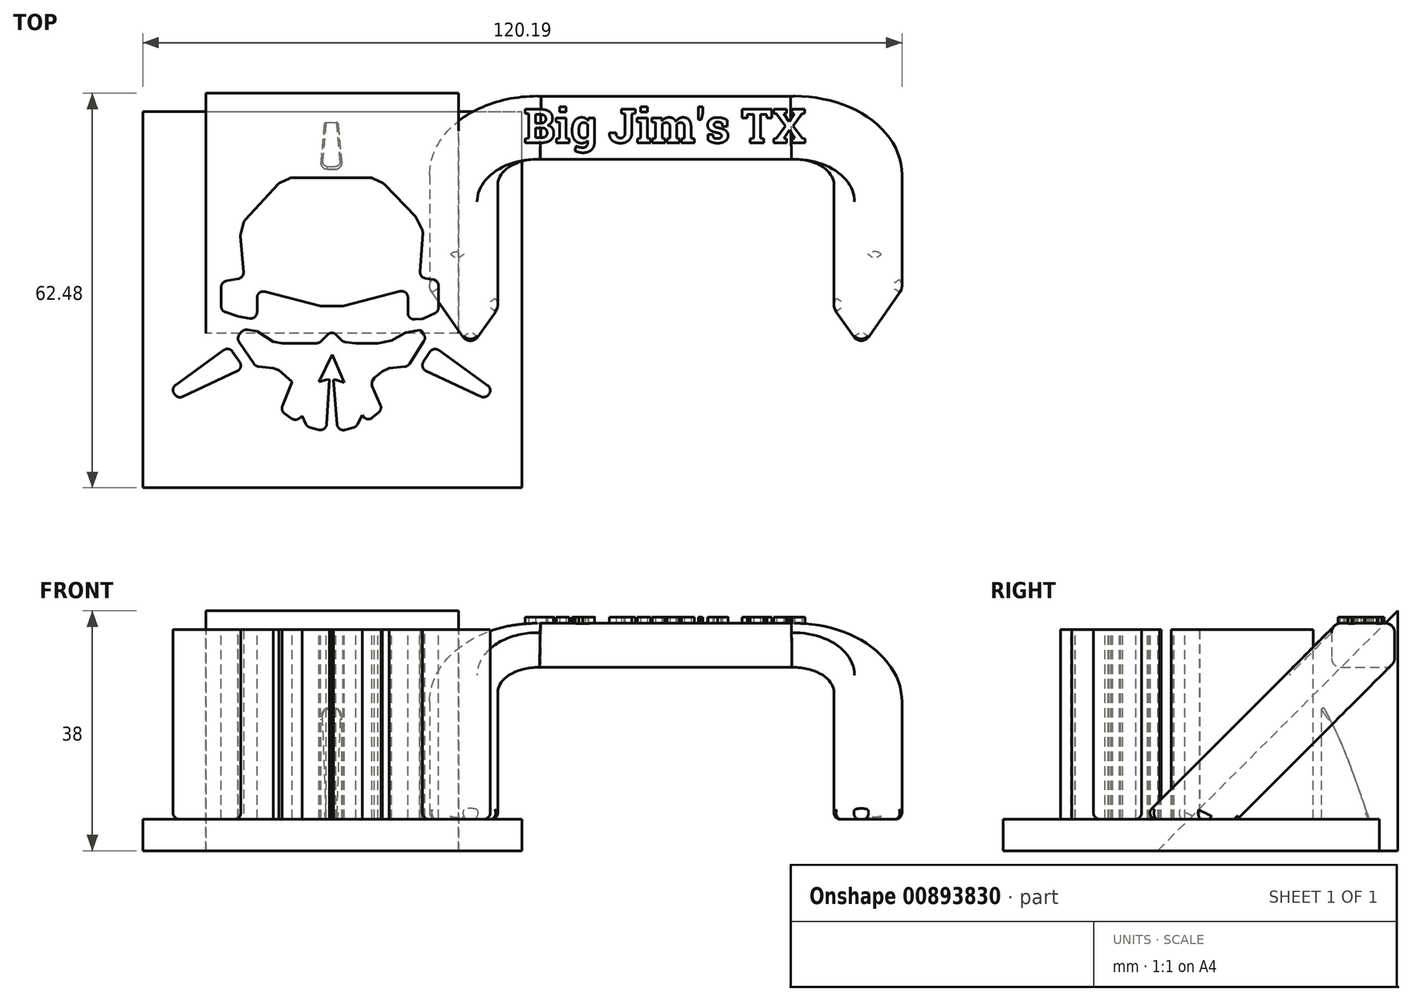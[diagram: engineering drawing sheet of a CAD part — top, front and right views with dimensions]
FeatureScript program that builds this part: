
annotation { "Feature Type Name" : "Feature", "Feature Type Description" : "" }
export const myFeature = defineFeature(function(context is Context, id is Id, definition is map)
    precondition{}
    {
        {
            var Q0;
            Q0=qCreatedBy(makeId("Front.planeOp"),FACE);
            var sketch = newSketch(context, id + "F0", { "sketchPlane" : qUnion([Q0])});
            skLineSegment(sketch, "E0", {"start": v(0, 0) * mm, "end": v(24, 0) * mm});
            skLineSegment(sketch, "E1", {"start": v(27, 5) * mm, "end": v(24, 0) * mm});
            skLineSegment(sketch, "E2", {"start": v(27, 5) * mm, "end": v(28.5, 5) * mm});
            skLineSegment(sketch, "E3", {"start": v(0, 35) * mm, "end": v(0, 0) * mm});
            skFitSpline(sketch, "E4", {"points": [v(0, 35) * mm, v(9.06, 34) * mm, v(13.03, 32.01) * mm, v(20.35, 24.23) * mm, v(28.5, 5) * mm], "startDerivative": vector(43.74, -2.76) * mm, "endDerivative": vector(20.52, -60.26) * mm});
            skSolve(sketch);
        }
        {
            var Q0;
            Q0=qSketchRegion(id+"F0",true);
            var Q1;
            Q1=sQuery(id+"F0.wireOp",EDGE,"E3");
            revolve(context, id + "F1", {"entities" : qUnion([Q0]), "axis" : qUnion([Q1]), "revolveType" : RevolveType.FULL});
        }
        {
            var Q0;
            Q0=qCreatedBy(makeId("Top.planeOp"),FACE);
            var sketch = newSketch(context, id + "F2", { "sketchPlane" : qUnion([Q0])});
            skCircle(sketch, "E5", {"center": v(0, 0) * mm, "radius": 5 * mm});
            skSolve(sketch);
        }
        {
            var Q0;
            Q0=qSketchRegion(id+"F2",true);
            extrude(context, id + "F3", {"entities" : qUnion([Q0]), "depth" : 32 * mm});
        }
        {
            var Q0;
            Q0=makeQuery(id+"F3.opExtrude","SWEPT_BODY",BODY,{"disambiguationData":[OSD([sQuery(id+"F2.wireOp",EDGE,"E5")])]});
            var Q1;
            Q1=makeQuery(id+"F1.opRevolve","SWEPT_BODY",BODY,{"disambiguationData":[OSD([sQuery(id+"F0.wireOp",EDGE,"E0"),sQuery(id+"F0.wireOp",EDGE,"E1"),sQuery(id+"F0.wireOp",EDGE,"E2"),sQuery(id+"F0.wireOp",EDGE,"3aklZLSy-hCqH-fZIi-s1VG-uW10MH76g0WD"),sQuery(id+"F0.wireOp",EDGE,"wuCtKPpf-We7b-kOsq-7vQO-teLjAkYNJH5X"),sQuery(id+"F0.wireOp",EDGE,"E3")])]});
            booleanBodies(context, id + "F4", {"operationType" : BooleanOperationType.SUBTRACTION, "tools" : qUnion([Q0]), "targets" : qUnion([Q1])});
        }
        {
            var Q0;
            Q0=qCreatedBy(makeId("Top.planeOp"),FACE);
            cPlane(context, id + "F5", {"entities" : qUnion([Q0]), "cplaneType" : CPlaneType.OFFSET, "offset" : 35 * mm, "width" : 150 * mm, "height" : 150 * mm});
        }
        {
            var Q0;
            Q0=qCreatedBy(id+"F5.planeOp",FACE);
            var sketch = newSketch(context, id + "F6", { "sketchPlane" : qUnion([Q0])});
            skLineSegment(sketch, "E6", {"start": v(-1.9, 20.95) * mm, "end": v(1.57, 20.95) * mm});
            skLineSegment(sketch, "E7", {"start": v(1.57, 20.95) * mm, "end": v(0.85, 28.83) * mm});
            skLineSegment(sketch, "E8", {"start": v(0.85, 28.83) * mm, "end": v(-1.17, 28.83) * mm});
            skLineSegment(sketch, "E9", {"start": v(-1.17, 28.83) * mm, "end": v(-1.9, 20.95) * mm});
            skLineSegment(sketch, "E10", {"start": v(-16.39, -7.1) * mm, "end": v(-14, -10.52) * mm});
            skLineSegment(sketch, "E11", {"start": v(-14, -10.52) * mm, "end": v(-24.43, -15.42) * mm});
            skLineSegment(sketch, "E12", {"start": v(-24.43, -15.42) * mm, "end": v(-25.63, -13.79) * mm});
            skLineSegment(sketch, "E13", {"start": v(-25.63, -13.79) * mm, "end": v(-16.39, -7.1) * mm});
            skLineSegment(sketch, "E14", {"start": v(16, -7.1) * mm, "end": v(13.8, -10.52) * mm});
            skLineSegment(sketch, "E15", {"start": v(13.8, -10.52) * mm, "end": v(24.28, -15.42) * mm});
            skLineSegment(sketch, "E16", {"start": v(24.28, -15.42) * mm, "end": v(25.36, -13.83) * mm});
            skLineSegment(sketch, "E17", {"start": v(25.36, -13.83) * mm, "end": v(16, -7.1) * mm});
            skLineSegment(sketch, "E18", {"start": v(-14, -4.39) * mm, "end": v(-11.93, -4.7) * mm});
            skLineSegment(sketch, "E19", {"start": v(-11.93, -4.7) * mm, "end": v(-9.33, -6.37) * mm});
            skLineSegment(sketch, "E20", {"start": v(-9.33, -6.37) * mm, "end": v(-7.9, -6.6) * mm});
            skLineSegment(sketch, "E21", {"start": v(-7.9, -6.6) * mm, "end": v(-4.54, -6.6) * mm});
            skLineSegment(sketch, "E22", {"start": v(-4.54, -6.6) * mm, "end": v(-2.11, -6.6) * mm});
            skLineSegment(sketch, "E23", {"start": v(-2.11, -6.6) * mm, "end": v(-0.46, -4.94) * mm});
            skLineSegment(sketch, "E24", {"start": v(-0.46, -4.94) * mm, "end": v(0.27, -4.94) * mm});
            skLineSegment(sketch, "E25", {"start": v(0.27, -4.94) * mm, "end": v(1.71, -6.37) * mm});
            skLineSegment(sketch, "E26", {"start": v(1.71, -6.37) * mm, "end": v(3.7, -6.6) * mm});
            skLineSegment(sketch, "E27", {"start": v(3.7, -6.6) * mm, "end": v(7.21, -6.6) * mm});
            skLineSegment(sketch, "E28", {"start": v(7.21, -6.6) * mm, "end": v(9.38, -6.15) * mm});
            skLineSegment(sketch, "E29", {"start": v(9.38, -6.15) * mm, "end": v(11.55, -4.94) * mm});
            skLineSegment(sketch, "E30", {"start": v(11.55, -4.94) * mm, "end": v(13.8, -4.5) * mm});
            skLineSegment(sketch, "E31", {"start": v(13.8, -4.5) * mm, "end": v(14.13, -4.7) * mm});
            skLineSegment(sketch, "E32", {"start": v(14.13, -4.7) * mm, "end": v(14.83, -5.76) * mm});
            skLineSegment(sketch, "E33", {"start": v(14.83, -5.76) * mm, "end": v(11.96, -10.26) * mm});
            skLineSegment(sketch, "E34", {"start": v(11.96, -10.26) * mm, "end": v(8.97, -10.52) * mm});
            skLineSegment(sketch, "E35", {"start": v(8.97, -10.52) * mm, "end": v(7.91, -11.03) * mm});
            skLineSegment(sketch, "E36", {"start": v(7.91, -11.03) * mm, "end": v(6.67, -12.1) * mm});
            skLineSegment(sketch, "E37", {"start": v(6.67, -12.1) * mm, "end": v(6.27, -12.72) * mm});
            skLineSegment(sketch, "E38", {"start": v(6.27, -12.72) * mm, "end": v(6.27, -13.33) * mm});
            skLineSegment(sketch, "E39", {"start": v(6.27, -13.33) * mm, "end": v(7.92, -17.05) * mm});
            skLineSegment(sketch, "E40", {"start": v(7.92, -17.05) * mm, "end": v(5.6, -19.03) * mm});
            skLineSegment(sketch, "E41", {"start": v(5.6, -19.03) * mm, "end": v(4.72, -18) * mm});
            skLineSegment(sketch, "E42", {"start": v(4.72, -18) * mm, "end": v(3.77, -19.83) * mm});
            skLineSegment(sketch, "E43", {"start": v(3.77, -19.83) * mm, "end": v(0.85, -20.66) * mm});
            skLineSegment(sketch, "E44", {"start": v(0.85, -20.66) * mm, "end": v(0.17, -12.4) * mm});
            skLineSegment(sketch, "E45", {"start": v(0.17, -12.4) * mm, "end": v(0.54, -12.37) * mm});
            skLineSegment(sketch, "E46", {"start": v(0.54, -12.37) * mm, "end": v(1.91, -12.83) * mm});
            skLineSegment(sketch, "E47", {"start": v(1.91, -12.83) * mm, "end": v(0, -8.41) * mm});
            skLineSegment(sketch, "E48", {"start": v(0, -8.41) * mm, "end": v(-2.11, -12.7) * mm});
            skLineSegment(sketch, "E49", {"start": v(-2.11, -12.7) * mm, "end": v(-0.97, -12.4) * mm});
            skLineSegment(sketch, "E50", {"start": v(-0.97, -12.4) * mm, "end": v(-0.46, -12.36) * mm});
            skLineSegment(sketch, "E51", {"start": v(-0.46, -12.36) * mm, "end": v(-0.97, -20.6) * mm});
            skLineSegment(sketch, "E52", {"start": v(-0.97, -20.6) * mm, "end": v(-3.99, -19.83) * mm});
            skLineSegment(sketch, "E53", {"start": v(-3.99, -19.83) * mm, "end": v(-4.79, -18.1) * mm});
            skLineSegment(sketch, "E54", {"start": v(-4.79, -18.1) * mm, "end": v(-5.8, -19) * mm});
            skLineSegment(sketch, "E55", {"start": v(-5.8, -19) * mm, "end": v(-8.2, -17.27) * mm});
            skLineSegment(sketch, "E56", {"start": v(-8.2, -17.27) * mm, "end": v(-6.4, -12.7) * mm});
            skLineSegment(sketch, "E57", {"start": v(-6.4, -12.7) * mm, "end": v(-8.47, -10.86) * mm});
            skLineSegment(sketch, "E58", {"start": v(-8.47, -10.86) * mm, "end": v(-9.33, -10.52) * mm});
            skLineSegment(sketch, "E59", {"start": v(-9.33, -10.52) * mm, "end": v(-12.14, -10.26) * mm});
            skLineSegment(sketch, "E60", {"start": v(-12.14, -10.26) * mm, "end": v(-15.2, -5.76) * mm});
            skLineSegment(sketch, "E61", {"start": v(-15.2, -5.76) * mm, "end": v(-14, -4.39) * mm});
            skLineSegment(sketch, "E62", {"start": v(-11.93, -2.85) * mm, "end": v(-14.9, -2.39) * mm});
            skLineSegment(sketch, "E63", {"start": v(-14.9, -2.39) * mm, "end": v(-17.6, -1.45) * mm});
            skLineSegment(sketch, "E64", {"start": v(-17.6, -1.45) * mm, "end": v(-17.6, 3.13) * mm});
            skLineSegment(sketch, "E65", {"start": v(-17.6, 3.13) * mm, "end": v(-14, 3.76) * mm});
            skLineSegment(sketch, "E66", {"start": v(-14, 3.76) * mm, "end": v(-14.56, 10.53) * mm});
            skLineSegment(sketch, "E67", {"start": v(-14.56, 10.53) * mm, "end": v(-14, 12.73) * mm});
            skLineSegment(sketch, "E68", {"start": v(-14, 12.73) * mm, "end": v(-8.4, 18.78) * mm});
            skLineSegment(sketch, "E69", {"start": v(-8.4, 18.78) * mm, "end": v(-6.64, 19.6) * mm});
            skLineSegment(sketch, "E70", {"start": v(-6.64, 19.6) * mm, "end": v(6.27, 19.6) * mm});
            skLineSegment(sketch, "E71", {"start": v(6.27, 19.6) * mm, "end": v(8.13, 18.7) * mm});
            skLineSegment(sketch, "E72", {"start": v(8.13, 18.7) * mm, "end": v(13.27, 13.32) * mm});
            skLineSegment(sketch, "E73", {"start": v(13.27, 13.32) * mm, "end": v(14.35, 11.03) * mm});
            skLineSegment(sketch, "E74", {"start": v(14.35, 11.03) * mm, "end": v(13.8, 3.84) * mm});
            skLineSegment(sketch, "E75", {"start": v(13.8, 3.84) * mm, "end": v(16.8, 3.38) * mm});
            skLineSegment(sketch, "E76", {"start": v(16.8, 3.38) * mm, "end": v(16.8, -1.57) * mm});
            skLineSegment(sketch, "E77", {"start": v(16.8, -1.57) * mm, "end": v(14.4, -2.7) * mm});
            skLineSegment(sketch, "E78", {"start": v(14.4, -2.7) * mm, "end": v(11.96, -2.9) * mm});
            skLineSegment(sketch, "E79", {"start": v(11.96, -2.9) * mm, "end": v(11.96, 1.93) * mm});
            skLineSegment(sketch, "E80", {"start": v(11.96, 1.93) * mm, "end": v(1.71, -0.7) * mm});
            skLineSegment(sketch, "E81", {"start": v(1.71, -0.7) * mm, "end": v(-1.9, -0.7) * mm});
            skLineSegment(sketch, "E82", {"start": v(-1.9, -0.7) * mm, "end": v(-11.93, 1.9) * mm});
            skLineSegment(sketch, "E83", {"start": v(-11.93, 1.9) * mm, "end": v(-11.93, -2.85) * mm});
            skSolve(sketch);
        }
        {
            var Q0;
            Q0=qSketchRegion(id+"F6",true);
            extrude(context, id + "F7", {"entities" : qUnion([Q0]), "oppositeDirection" : true, "depth" : 30 * mm});
        }
        {
            var Q0;
            Q0=qCreatedBy(makeId("Right.planeOp"),FACE);
            var sketch = newSketch(context, id + "F8", { "sketchPlane" : qUnion([Q0])});
            skLineSegment(sketch, "E84.bottom", {"start": v(-29.48, 5) * mm, "end": v(30.12, 5) * mm});
            skLineSegment(sketch, "E84.top", {"start": v(-29.48, 0) * mm, "end": v(30.12, 0) * mm});
            skLineSegment(sketch, "E84.left", {"start": v(-29.48, 5) * mm, "end": v(-29.48, 0) * mm});
            skLineSegment(sketch, "E84.right", {"start": v(30.12, 5) * mm, "end": v(30.12, 0) * mm});
            skSolve(sketch);
        }
        {
            var Q0;
            Q0=makeQuery(id+"F7.opExtrude","SWEPT_EDGE",EDGE,{"disambiguationData":[OSD([sQuery(id+"F6.wireOp",EDGE,"E10"),sQuery(id+"F6.wireOp",EDGE,"E11")])]});
            var Q1;
            Q1=makeQuery(id+"F7.opExtrude","SWEPT_EDGE",EDGE,{"disambiguationData":[OSD([sQuery(id+"F6.wireOp",EDGE,"E59"),sQuery(id+"F6.wireOp",EDGE,"E60")])]});
            var Q2;
            Q2=makeQuery(id+"F7.opExtrude","SWEPT_EDGE",EDGE,{"disambiguationData":[OSD([sQuery(id+"F6.wireOp",EDGE,"E60"),sQuery(id+"F6.wireOp",EDGE,"E61")])]});
            var Q3;
            Q3=makeQuery(id+"F7.opExtrude","SWEPT_EDGE",EDGE,{"disambiguationData":[OSD([sQuery(id+"F6.wireOp",EDGE,"E33"),sQuery(id+"F6.wireOp",EDGE,"E34")])]});
            var Q4;
            Q4=makeQuery(id+"F7.opExtrude","SWEPT_EDGE",EDGE,{"disambiguationData":[OSD([sQuery(id+"F6.wireOp",EDGE,"E14"),sQuery(id+"F6.wireOp",EDGE,"E15")])]});
            var Q5;
            Q5=makeQuery(id+"F7.opExtrude","SWEPT_EDGE",EDGE,{"disambiguationData":[OSD([sQuery(id+"F6.wireOp",EDGE,"E39"),sQuery(id+"F6.wireOp",EDGE,"E40")])]});
            var Q6;
            Q6=makeQuery(id+"F7.opExtrude","SWEPT_EDGE",EDGE,{"disambiguationData":[OSD([sQuery(id+"F6.wireOp",EDGE,"E55"),sQuery(id+"F6.wireOp",EDGE,"E56")])]});
            var Q7;
            Q7=makeQuery(id+"F7.opExtrude","SWEPT_EDGE",EDGE,{"disambiguationData":[OSD([sQuery(id+"F6.wireOp",EDGE,"E51"),sQuery(id+"F6.wireOp",EDGE,"E52")])]});
            var Q8;
            Q8=makeQuery(id+"F7.opExtrude","SWEPT_EDGE",EDGE,{"disambiguationData":[OSD([sQuery(id+"F6.wireOp",EDGE,"E43"),sQuery(id+"F6.wireOp",EDGE,"E44")])]});
            var Q9;
            Q9=makeQuery(id+"F7.opExtrude","SWEPT_EDGE",EDGE,{"disambiguationData":[OSD([sQuery(id+"F6.wireOp",EDGE,"E42"),sQuery(id+"F6.wireOp",EDGE,"E43")])]});
            var Q10;
            Q10=makeQuery(id+"F7.opExtrude","SWEPT_EDGE",EDGE,{"disambiguationData":[OSD([sQuery(id+"F6.wireOp",EDGE,"E52"),sQuery(id+"F6.wireOp",EDGE,"E53")])]});
            var Q11;
            Q11=makeQuery(id+"F7.opExtrude","SWEPT_EDGE",EDGE,{"disambiguationData":[OSD([sQuery(id+"F6.wireOp",EDGE,"E54"),sQuery(id+"F6.wireOp",EDGE,"E55")])]});
            var Q12;
            Q12=makeQuery(id+"F7.opExtrude","SWEPT_EDGE",EDGE,{"disambiguationData":[OSD([sQuery(id+"F6.wireOp",EDGE,"E40"),sQuery(id+"F6.wireOp",EDGE,"E41")])]});
            var Q13;
            Q13=makeQuery(id+"F7.opExtrude","SWEPT_EDGE",EDGE,{"disambiguationData":[OSD([sQuery(id+"F6.wireOp",EDGE,"E32"),sQuery(id+"F6.wireOp",EDGE,"E33")])]});
            var Q14;
            Q14=makeQuery(id+"F7.opExtrude","SWEPT_EDGE",EDGE,{"disambiguationData":[OSD([sQuery(id+"F6.wireOp",EDGE,"E14"),sQuery(id+"F6.wireOp",EDGE,"E17")])]});
            var Q15;
            Q15=makeQuery(id+"F7.opExtrude","SWEPT_EDGE",EDGE,{"disambiguationData":[OSD([sQuery(id+"F6.wireOp",EDGE,"E10"),sQuery(id+"F6.wireOp",EDGE,"E13")])]});
            var Q16;
            Q16=makeQuery(id+"F7.opExtrude","SWEPT_EDGE",EDGE,{"disambiguationData":[OSD([sQuery(id+"F6.wireOp",EDGE,"E18"),sQuery(id+"F6.wireOp",EDGE,"E61")])]});
            var Q17;
            Q17=makeQuery(id+"F7.opExtrude","SWEPT_EDGE",EDGE,{"disambiguationData":[OSD([sQuery(id+"F6.wireOp",EDGE,"E22"),sQuery(id+"F6.wireOp",EDGE,"E23")])]});
            var Q18;
            Q18=makeQuery(id+"F7.opExtrude","SWEPT_EDGE",EDGE,{"disambiguationData":[OSD([sQuery(id+"F6.wireOp",EDGE,"E24"),sQuery(id+"F6.wireOp",EDGE,"E25")])]});
            var Q19;
            Q19=makeQuery(id+"F7.opExtrude","SWEPT_EDGE",EDGE,{"disambiguationData":[OSD([sQuery(id+"F6.wireOp",EDGE,"E25"),sQuery(id+"F6.wireOp",EDGE,"E26")])]});
            var Q20;
            Q20=makeQuery(id+"F7.opExtrude","SWEPT_EDGE",EDGE,{"disambiguationData":[OSD([sQuery(id+"F6.wireOp",EDGE,"E29"),sQuery(id+"F6.wireOp",EDGE,"E30")])]});
            var Q21;
            Q21=makeQuery(id+"F7.opExtrude","SWEPT_EDGE",EDGE,{"disambiguationData":[OSD([sQuery(id+"F6.wireOp",EDGE,"E6"),sQuery(id+"F6.wireOp",EDGE,"E7")])]});
            var Q22;
            Q22=makeQuery(id+"F7.opExtrude","SWEPT_EDGE",EDGE,{"disambiguationData":[OSD([sQuery(id+"F6.wireOp",EDGE,"E6"),sQuery(id+"F6.wireOp",EDGE,"E9")])]});
            var Q23;
            Q23=makeQuery(id+"F7.opExtrude","SWEPT_EDGE",EDGE,{"disambiguationData":[OSD([sQuery(id+"F6.wireOp",EDGE,"E69"),sQuery(id+"F6.wireOp",EDGE,"E70")])]});
            var Q24;
            Q24=makeQuery(id+"F7.opExtrude","SWEPT_EDGE",EDGE,{"disambiguationData":[OSD([sQuery(id+"F6.wireOp",EDGE,"E68"),sQuery(id+"F6.wireOp",EDGE,"E69")])]});
            var Q25;
            Q25=makeQuery(id+"F7.opExtrude","SWEPT_EDGE",EDGE,{"disambiguationData":[OSD([sQuery(id+"F6.wireOp",EDGE,"E70"),sQuery(id+"F6.wireOp",EDGE,"E71")])]});
            var Q26;
            Q26=makeQuery(id+"F7.opExtrude","SWEPT_EDGE",EDGE,{"disambiguationData":[OSD([sQuery(id+"F6.wireOp",EDGE,"E71"),sQuery(id+"F6.wireOp",EDGE,"E72")])]});
            var Q27;
            Q27=makeQuery(id+"F7.opExtrude","SWEPT_EDGE",EDGE,{"disambiguationData":[OSD([sQuery(id+"F6.wireOp",EDGE,"E67"),sQuery(id+"F6.wireOp",EDGE,"E68")])]});
            var Q28;
            Q28=makeQuery(id+"F7.opExtrude","SWEPT_EDGE",EDGE,{"disambiguationData":[OSD([sQuery(id+"F6.wireOp",EDGE,"E66"),sQuery(id+"F6.wireOp",EDGE,"E67")])]});
            var Q29;
            Q29=makeQuery(id+"F7.opExtrude","SWEPT_EDGE",EDGE,{"disambiguationData":[OSD([sQuery(id+"F6.wireOp",EDGE,"E65"),sQuery(id+"F6.wireOp",EDGE,"E66")])]});
            var Q30;
            Q30=makeQuery(id+"F7.opExtrude","SWEPT_EDGE",EDGE,{"disambiguationData":[OSD([sQuery(id+"F6.wireOp",EDGE,"E64"),sQuery(id+"F6.wireOp",EDGE,"E65")])]});
            var Q31;
            Q31=makeQuery(id+"F7.opExtrude","SWEPT_EDGE",EDGE,{"disambiguationData":[OSD([sQuery(id+"F6.wireOp",EDGE,"E63"),sQuery(id+"F6.wireOp",EDGE,"E64")])]});
            var Q32;
            Q32=makeQuery(id+"F7.opExtrude","SWEPT_EDGE",EDGE,{"disambiguationData":[OSD([sQuery(id+"F6.wireOp",EDGE,"E62"),sQuery(id+"F6.wireOp",EDGE,"E83")])]});
            var Q33;
            Q33=makeQuery(id+"F7.opExtrude","SWEPT_EDGE",EDGE,{"disambiguationData":[OSD([sQuery(id+"F6.wireOp",EDGE,"E82"),sQuery(id+"F6.wireOp",EDGE,"E83")])]});
            var Q34;
            Q34=makeQuery(id+"F7.opExtrude","SWEPT_EDGE",EDGE,{"disambiguationData":[OSD([sQuery(id+"F6.wireOp",EDGE,"E78"),sQuery(id+"F6.wireOp",EDGE,"E79")])]});
            var Q35;
            Q35=makeQuery(id+"F7.opExtrude","SWEPT_EDGE",EDGE,{"disambiguationData":[OSD([sQuery(id+"F6.wireOp",EDGE,"E77"),sQuery(id+"F6.wireOp",EDGE,"E78")])]});
            var Q36;
            Q36=makeQuery(id+"F7.opExtrude","SWEPT_EDGE",EDGE,{"disambiguationData":[OSD([sQuery(id+"F6.wireOp",EDGE,"E76"),sQuery(id+"F6.wireOp",EDGE,"E77")])]});
            var Q37;
            Q37=makeQuery(id+"F7.opExtrude","SWEPT_EDGE",EDGE,{"disambiguationData":[OSD([sQuery(id+"F6.wireOp",EDGE,"E75"),sQuery(id+"F6.wireOp",EDGE,"E76")])]});
            var Q38;
            Q38=makeQuery(id+"F7.opExtrude","SWEPT_EDGE",EDGE,{"disambiguationData":[OSD([sQuery(id+"F6.wireOp",EDGE,"E74"),sQuery(id+"F6.wireOp",EDGE,"E75")])]});
            var Q39;
            Q39=makeQuery(id+"F7.opExtrude","SWEPT_EDGE",EDGE,{"disambiguationData":[OSD([sQuery(id+"F6.wireOp",EDGE,"E73"),sQuery(id+"F6.wireOp",EDGE,"E74")])]});
            var Q40;
            Q40=makeQuery(id+"F7.opExtrude","SWEPT_EDGE",EDGE,{"disambiguationData":[OSD([sQuery(id+"F6.wireOp",EDGE,"E72"),sQuery(id+"F6.wireOp",EDGE,"E73")])]});
            var Q41;
            Q41=makeQuery(id+"F7.opExtrude","SWEPT_EDGE",EDGE,{"disambiguationData":[OSD([sQuery(id+"F6.wireOp",EDGE,"E79"),sQuery(id+"F6.wireOp",EDGE,"E80")])]});
            var Q42;
            Q42=makeQuery(id+"F7.opExtrude","SWEPT_EDGE",EDGE,{"disambiguationData":[OSD([sQuery(id+"F6.wireOp",EDGE,"E23"),sQuery(id+"F6.wireOp",EDGE,"E24")])]});
            var Q43;
            Q43=makeQuery(id+"F7.opExtrude","SWEPT_EDGE",EDGE,{"disambiguationData":[OSD([sQuery(id+"F6.wireOp",EDGE,"E11"),sQuery(id+"F6.wireOp",EDGE,"E12")])]});
            var Q44;
            Q44=makeQuery(id+"F7.opExtrude","SWEPT_EDGE",EDGE,{"disambiguationData":[OSD([sQuery(id+"F6.wireOp",EDGE,"E12"),sQuery(id+"F6.wireOp",EDGE,"E13")])]});
            var Q45;
            Q45=makeQuery(id+"F7.opExtrude","SWEPT_EDGE",EDGE,{"disambiguationData":[OSD([sQuery(id+"F6.wireOp",EDGE,"E15"),sQuery(id+"F6.wireOp",EDGE,"E16")])]});
            var Q46;
            Q46=makeQuery(id+"F7.opExtrude","SWEPT_EDGE",EDGE,{"disambiguationData":[OSD([sQuery(id+"F6.wireOp",EDGE,"E16"),sQuery(id+"F6.wireOp",EDGE,"E17")])]});
            var Q47;
            Q47=makeQuery(id+"F7.opExtrude","SWEPT_EDGE",EDGE,{"disambiguationData":[OSD([sQuery(id+"F6.wireOp",EDGE,"E8"),sQuery(id+"F6.wireOp",EDGE,"E9")])]});
            var Q48;
            Q48=makeQuery(id+"F7.opExtrude","SWEPT_EDGE",EDGE,{"disambiguationData":[OSD([sQuery(id+"F6.wireOp",EDGE,"E7"),sQuery(id+"F6.wireOp",EDGE,"E8")])]});
            fillet(context, id + "F9", {"entities" : qUnion([Q0, Q1, Q2, Q3, Q4, Q5, Q6, Q7, Q8, Q9, Q10, Q11, Q12, Q13, Q14, Q15, Q16, Q17, Q18, Q19, Q20, Q21, Q22, Q23, Q24, Q25, Q26, Q27, Q28, Q29, Q30, Q31, Q32, Q33, Q34, Q35, Q36, Q37, Q38, Q39, Q40, Q41, Q42, Q43, Q44, Q45, Q46, Q47, Q48]), "radius" : 1 * mm, "tangentPropagation" : true, "allowEdgeOverflow" : false});
        }
        {
            var Q0;
            Q0=qSketchRegion(id+"F8",true);
            extrude(context, id + "F10", {"entities" : qUnion([Q0]), "oppositeDirection" : true, "depth" : 60 * mm, "symmetric" : true});
        }
        {
            var Q0;
            Q0=makeQuery(id+"F1.opRevolve","SWEPT_BODY",BODY,{"disambiguationData":[OSD([sQuery(id+"F0.wireOp",EDGE,"E0"),sQuery(id+"F0.wireOp",EDGE,"E1"),sQuery(id+"F0.wireOp",EDGE,"E2"),sQuery(id+"F0.wireOp",EDGE,"3aklZLSy-hCqH-fZIi-s1VG-uW10MH76g0WD"),sQuery(id+"F0.wireOp",EDGE,"wuCtKPpf-We7b-kOsq-7vQO-teLjAkYNJH5X"),sQuery(id+"F0.wireOp",EDGE,"E3")])]});
            var Q1;
            Q1=makeQuery(id+"F7.opExtrude","SWEPT_BODY",BODY,{"disambiguationData":[OSD([sQuery(id+"F6.wireOp",EDGE,"E6"),sQuery(id+"F6.wireOp",EDGE,"E7"),sQuery(id+"F6.wireOp",EDGE,"E8"),sQuery(id+"F6.wireOp",EDGE,"E9")])]});
            booleanBodies(context, id + "F11", {"operationType" : BooleanOperationType.INTERSECTION, "tools" : qUnion([Q0, Q1])});
        }
        {
            var Q0;
            Q0=qCreatedBy(makeId("Right.planeOp"),FACE);
            cPlane(context, id + "F12", {"entities" : qUnion([Q0]), "cplaneType" : CPlaneType.OFFSET, "offset" : 52.8 * mm, "width" : 150 * mm, "height" : 150 * mm});
        }
        {
            var Q0;
            {var subQ0=sQuery(id+"F0.wireOp",EDGE,"E2");var subQ1=sQuery(id+"F6.wireOp",EDGE,"E16");var subQ2=sQuery(id+"F0.wireOp",EDGE,"E4");Q0=makeQuery(id+"F11.opBoolean","SPLIT",EDGE,{"disambiguationData":[TD([makeQuery(id+"F9.opFillet","BLEND_FACE",FACE,{"disambiguationData":[OSD([sQuery(id+"F6.wireOp",EDGE,"E15"),subQ1])]})])],"derivedFrom":makeQuery(id+"F1.opRevolve","SWEPT_EDGE",EDGE,{"disambiguationData":[OSD([subQ0,subQ2])]})});}
            var Q1;
            Q1=makeQuery(id+"F11.opBoolean","INTERSECT",EDGE,{"derivedFrom":[makeQuery(id+"F1.opRevolve","SWEPT_FACE",FACE,{"disambiguationData":[OSD([sQuery(id+"F0.wireOp",EDGE,"E4")])]}),makeQuery(id+"F7.opExtrude","SWEPT_FACE",FACE,{"disambiguationData":[OSD([sQuery(id+"F6.wireOp",EDGE,"E14")])]})]});
            var Q2;
            {var subQ0=sQuery(id+"F0.wireOp",EDGE,"E2");var subQ1=sQuery(id+"F0.wireOp",EDGE,"E4");var subQ2=sQuery(id+"F6.wireOp",EDGE,"E12");Q2=makeQuery(id+"F11.opBoolean","SPLIT",EDGE,{"disambiguationData":[TD([makeQuery(id+"F9.opFillet","BLEND_FACE",FACE,{"disambiguationData":[OSD([sQuery(id+"F6.wireOp",EDGE,"E11"),subQ2])]})])],"derivedFrom":makeQuery(id+"F1.opRevolve","SWEPT_EDGE",EDGE,{"disambiguationData":[OSD([subQ0,subQ1])]})});}
            var Q3;
            Q3=makeQuery(id+"F11.opBoolean","INTERSECT",EDGE,{"derivedFrom":[makeQuery(id+"F1.opRevolve","SWEPT_FACE",FACE,{"disambiguationData":[OSD([sQuery(id+"F0.wireOp",EDGE,"E4")])]}),makeQuery(id+"F7.opExtrude","SWEPT_FACE",FACE,{"disambiguationData":[OSD([sQuery(id+"F6.wireOp",EDGE,"E10")])]})]});
            var Q4;
            {var subQ0=sQuery(id+"F0.wireOp",EDGE,"E2");var subQ1=sQuery(id+"F0.wireOp",EDGE,"E4");var subQ2=sQuery(id+"F6.wireOp",EDGE,"E8");Q4=makeQuery(id+"F11.opBoolean","SPLIT",EDGE,{"disambiguationData":[TD([makeQuery(id+"F9.opFillet","BLEND_FACE",FACE,{"disambiguationData":[OSD([sQuery(id+"F6.wireOp",EDGE,"E7"),subQ2])]})])],"derivedFrom":makeQuery(id+"F1.opRevolve","SWEPT_EDGE",EDGE,{"disambiguationData":[OSD([subQ0,subQ1])]})});}
            var Q5;
            Q5=makeQuery(id+"F11.opBoolean","INTERSECT",EDGE,{"derivedFrom":[makeQuery(id+"F1.opRevolve","SWEPT_FACE",FACE,{"disambiguationData":[OSD([sQuery(id+"F0.wireOp",EDGE,"E4")])]}),makeQuery(id+"F7.opExtrude","SWEPT_FACE",FACE,{"disambiguationData":[OSD([sQuery(id+"F6.wireOp",EDGE,"E6")])]})]});
            var Q6;
            {var subQ16=sQuery(id+"F6.wireOp",EDGE,"E62");Q6=makeQuery(id+"F11.opBoolean","SPLIT",FACE,{"disambiguationData":[TD([makeQuery(id+"F7.opExtrude","SWEPT_FACE",FACE,{"disambiguationData":[OSD([subQ16])]})])],"derivedFrom":makeQuery(id+"F1.opRevolve","SWEPT_FACE",FACE,{"disambiguationData":[OSD([sQuery(id+"F0.wireOp",EDGE,"E4")])]})});}
            var Q7;
            {var subQ16=sQuery(id+"F6.wireOp",EDGE,"E18");Q7=makeQuery(id+"F11.opBoolean","SPLIT",FACE,{"disambiguationData":[TD([makeQuery(id+"F7.opExtrude","SWEPT_FACE",FACE,{"disambiguationData":[OSD([subQ16])]})])],"derivedFrom":makeQuery(id+"F1.opRevolve","SWEPT_FACE",FACE,{"disambiguationData":[OSD([sQuery(id+"F0.wireOp",EDGE,"E4")])]})});}
            fillet(context, id + "F13", {"entities" : qUnion([Q0, Q1, Q2, Q3, Q4, Q5, Q6, Q7]), "radius" : 0.25 * mm, "tangentPropagation" : true, "allowEdgeOverflow" : false});
        }
        {
            var Q0;
            {var subQ0=sQuery(id+"F6.wireOp",EDGE,"E11");Q0=makeQuery(id+"F11.opBoolean","SPLIT",EDGE,{"disambiguationData":[topologyDisambiguationEdgeConnected([makeQuery(id+"F10.opExtrude","SWEPT_FACE",FACE,{"disambiguationData":[OSD([sQuery(id+"F8.wireOp",EDGE,"E84.bottom")])]})])],"derivedFrom":makeQuery(id+"F7.opExtrude","CAP_EDGE",EDGE,{"disambiguationData":[OSD([subQ0])],"isStart":false})});}
            var Q1;
            {var subQ0=sQuery(id+"F6.wireOp",EDGE,"E15");Q1=makeQuery(id+"F11.opBoolean","SPLIT",EDGE,{"disambiguationData":[topologyDisambiguationEdgeConnected([makeQuery(id+"F10.opExtrude","SWEPT_FACE",FACE,{"disambiguationData":[OSD([sQuery(id+"F8.wireOp",EDGE,"E84.bottom")])]})])],"derivedFrom":makeQuery(id+"F7.opExtrude","CAP_EDGE",EDGE,{"disambiguationData":[OSD([subQ0])],"isStart":false})});}
            var Q2;
            {var subQ0=sQuery(id+"F6.wireOp",EDGE,"E9");Q2=makeQuery(id+"F11.opBoolean","SPLIT",EDGE,{"disambiguationData":[topologyDisambiguationEdgeConnected([makeQuery(id+"F10.opExtrude","SWEPT_FACE",FACE,{"disambiguationData":[OSD([sQuery(id+"F8.wireOp",EDGE,"E84.bottom")])]})])],"derivedFrom":makeQuery(id+"F7.opExtrude","CAP_EDGE",EDGE,{"disambiguationData":[OSD([subQ0])],"isStart":false})});}
            fillet(context, id + "F14", {"entities" : qUnion([Q0, Q1, Q2]), "radius" : 1 * mm, "tangentPropagation" : true, "allowEdgeOverflow" : false});
        }
        {
            var Q0;
            Q0=qCreatedBy(makeId("Right.planeOp"),FACE);
            var sketch = newSketch(context, id + "F15", { "sketchPlane" : qUnion([Q0])});
            skLineSegment(sketch, "E85", {"start": v(33, 0) * mm, "end": v(-5, 0) * mm});
            skLineSegment(sketch, "E86", {"start": v(-5, 0) * mm, "end": v(33, 38) * mm});
            skLineSegment(sketch, "E87", {"start": v(33, 38) * mm, "end": v(33, 0) * mm});
            skSolve(sketch);
        }
        {
            var Q0;
            Q0 = qSketchRegion(id + "F15", true);
            extrude(context, id + "F16", {"entities" : qUnion([Q0]), "depth" : 40 * mm, "offsetDistance" : 25 * mm, "symmetric" : true});
        }
        {
            var Q0;
            Q0=makeQuery(id+"F16.opExtrude","SWEPT_FACE",FACE,{"disambiguationData":[OSD([sQuery(id+"F15.wireOp",EDGE,"E86")])]});
            var sketch = newSketch(context, id + "F17", { "sketchPlane" : qUnion([Q0])});
            skLineSegment(sketch, "E88", {"start": v(20.8, -3.54) * mm, "end": v(20.8, 30.84) * mm});
            skLineSegment(sketch, "E89", {"start": v(52.8, 42.46) * mm, "end": v(32.94, 42.46) * mm});
            skArc(sketch, "E90", {"start": v(32.94, 42.46) * mm, "mid": v(24.39, 39.25) * mm, "end": v(20.8, 30.84) * mm});
            skSolve(sketch);
        }
        {
            var Q0;
            Q0=qCreatedBy(id+"F12.planeOp",FACE);
            var sketch = newSketch(context, id + "F18", { "sketchPlane" : qUnion([Q0])});
            skLineSegment(sketch, "E91.bottom", {"start": v(24.03, 36.03) * mm, "end": v(31.03, 36.03) * mm});
            skLineSegment(sketch, "E91.top", {"start": v(24.03, 29.03) * mm, "end": v(31.03, 29.03) * mm});
            skLineSegment(sketch, "E91.left", {"start": v(22.53, 34.53) * mm, "end": v(22.53, 30.53) * mm});
            skLineSegment(sketch, "E91.right", {"start": v(32.53, 34.53) * mm, "end": v(32.53, 30.53) * mm});
            skPoint(sketch, "E92.visualSharp", {"position": v(22.53, 36.03) * mm});
            skArc(sketch, "E92.filletArc", {"start": v(24.03, 36.03) * mm, "mid": v(22.97, 35.59) * mm, "end": v(22.53, 34.53) * mm});
            skPoint(sketch, "E93.visualSharp", {"position": v(22.53, 29.03) * mm});
            skArc(sketch, "E93.filletArc", {"start": v(22.53, 30.53) * mm, "mid": v(22.97, 29.47) * mm, "end": v(24.03, 29.03) * mm});
            skPoint(sketch, "E94.visualSharp", {"position": v(32.53, 29.03) * mm});
            skArc(sketch, "E94.filletArc", {"start": v(31.03, 29.03) * mm, "mid": v(32.09, 29.47) * mm, "end": v(32.53, 30.53) * mm});
            skPoint(sketch, "E95.visualSharp", {"position": v(32.53, 36.03) * mm});
            skArc(sketch, "E95.filletArc", {"start": v(32.53, 34.53) * mm, "mid": v(32.09, 35.59) * mm, "end": v(31.03, 36.03) * mm});
            skSolve(sketch);
        }
        {
            var Q0;
            Q0=makeQuery(id+"F18.imprint","IMPRINT",FACE,{"disambiguationData":[TD([[makeQuery(id+"F18.imprint","IMPRINT",EDGE,{"derivedFrom":sQuery(id+"F18.wireOp",EDGE,"E91.bottom")}),-1.0]])]});
            var Q1;
            Q1=qConstructionFilter(qBodyType(qCreatedBy(id+"F17",EDGE),BodyType.WIRE),ConstructionObject.NO);
            sweep(context, id + "F19", {"profiles" : qUnion([Q0]), "path" : qUnion([Q1])});
        }
        {
            var Q0;
            Q0=qCreatedBy(makeId("Front.planeOp"),FACE);
            var sketch = newSketch(context, id + "F20", { "sketchPlane" : qUnion([Q0])});
            skLineSegment(sketch, "E96.bottom", {"start": v(0, -7) * mm, "end": v(30, -7) * mm});
            skLineSegment(sketch, "E96.top", {"start": v(0, 5) * mm, "end": v(30, 5) * mm});
            skLineSegment(sketch, "E96.left", {"start": v(0, -7) * mm, "end": v(0, 5) * mm});
            skLineSegment(sketch, "E96.right", {"start": v(30, -7) * mm, "end": v(30, 5) * mm});
            skSolve(sketch);
        }
        {
            var Q0;
            Q0 = qSketchRegion(id + "F20", true);
            extrude(context, id + "F21", {"entities" : qUnion([Q0]), "depth" : 25 * mm, "offsetDistance" : 25 * mm, "symmetric" : true});
        }
        {
            var Q0;
            Q0=makeQuery(id+"F21.opExtrude","SWEPT_BODY",BODY,{"disambiguationData":[OSD([sQuery(id+"F20.wireOp",EDGE,"E96.bottom"),sQuery(id+"F20.wireOp",EDGE,"E96.top"),sQuery(id+"F20.wireOp",EDGE,"E96.left"),sQuery(id+"F20.wireOp",EDGE,"E96.right")])]});
            var Q1;
            Q1=makeQuery(id+"F19.opSweep","SWEPT_BODY",BODY,{"disambiguationData":[OSD([sQuery(id+"F17.wireOp",EDGE,"E88"),sQuery(id+"F18.wireOp",EDGE,"E91.bottom"),sQuery(id+"F18.wireOp",EDGE,"E91.top"),sQuery(id+"F18.wireOp",EDGE,"E91.left"),sQuery(id+"F18.wireOp",EDGE,"E91.right"),sQuery(id+"F18.wireOp",EDGE,"E92.filletArc"),sQuery(id+"F18.wireOp",EDGE,"E93.filletArc"),sQuery(id+"F18.wireOp",EDGE,"E94.filletArc"),sQuery(id+"F18.wireOp",EDGE,"E95.filletArc")])]});
            booleanBodies(context, id + "F22", {"operationType" : BooleanOperationType.SUBTRACTION, "tools" : qUnion([Q0]), "targets" : qUnion([Q1])});
        }
        {
            var Q0;
            Q0=makeQuery(id+"F22.opBoolean","INTERSECT",EDGE,{"derivedFrom":[makeQuery(id+"F19.opSweep","SWEPT_FACE",FACE,{"disambiguationData":[OSD([sQuery(id+"F17.wireOp",EDGE,"E88"),sQuery(id+"F18.wireOp",EDGE,"E91.left")])]}),makeQuery(id+"F21.opExtrude","SWEPT_FACE",FACE,{"disambiguationData":[OSD([sQuery(id+"F20.wireOp",EDGE,"E96.top")])]})]});
            fillet(context, id + "F23", {"entities" : qUnion([Q0]), "radius" : 1 * mm, "tangentPropagation" : true, "allowEdgeOverflow" : false});
        }
        {
            var Q0;
            Q0=makeQuery(id+"F19.opSweep","SWEPT_BODY",BODY,{"disambiguationData":[OSD([sQuery(id+"F17.wireOp",EDGE,"E88"),sQuery(id+"F18.wireOp",EDGE,"E91.bottom"),sQuery(id+"F18.wireOp",EDGE,"E91.top"),sQuery(id+"F18.wireOp",EDGE,"E91.left"),sQuery(id+"F18.wireOp",EDGE,"E91.right"),sQuery(id+"F18.wireOp",EDGE,"E92.filletArc"),sQuery(id+"F18.wireOp",EDGE,"E93.filletArc"),sQuery(id+"F18.wireOp",EDGE,"E94.filletArc"),sQuery(id+"F18.wireOp",EDGE,"E95.filletArc")])]});
            var Q1;
            Q1=qCreatedBy(id+"F12.planeOp",FACE);
            mirror(context, id + "F24", {"entities" : qUnion([Q0]), "mirrorPlane" : qUnion([Q1])});
        }
        {
            var Q0;
            Q0=makeQuery(id+"F19.opSweep","SWEPT_BODY",BODY,{"disambiguationData":[OSD([sQuery(id+"F17.wireOp",EDGE,"E88"),sQuery(id+"F18.wireOp",EDGE,"E91.bottom"),sQuery(id+"F18.wireOp",EDGE,"E91.top"),sQuery(id+"F18.wireOp",EDGE,"E91.left"),sQuery(id+"F18.wireOp",EDGE,"E91.right"),sQuery(id+"F18.wireOp",EDGE,"E92.filletArc"),sQuery(id+"F18.wireOp",EDGE,"E93.filletArc"),sQuery(id+"F18.wireOp",EDGE,"E94.filletArc"),sQuery(id+"F18.wireOp",EDGE,"E95.filletArc")])]});
            var Q1;
            Q1=makeQuery(id+"F24.opPattern","COPY",BODY,{"derivedFrom":makeQuery(id+"F19.opSweep","SWEPT_BODY",BODY,{"disambiguationData":[OSD([sQuery(id+"F17.wireOp",EDGE,"E88"),sQuery(id+"F18.wireOp",EDGE,"E91.bottom"),sQuery(id+"F18.wireOp",EDGE,"E91.top"),sQuery(id+"F18.wireOp",EDGE,"E91.left"),sQuery(id+"F18.wireOp",EDGE,"E91.right"),sQuery(id+"F18.wireOp",EDGE,"E92.filletArc"),sQuery(id+"F18.wireOp",EDGE,"E93.filletArc"),sQuery(id+"F18.wireOp",EDGE,"E94.filletArc"),sQuery(id+"F18.wireOp",EDGE,"E95.filletArc")])]}),"instanceName":"1"});
            booleanBodies(context, id + "F25", {"operationType" : BooleanOperationType.UNION, "tools" : qUnion([Q0, Q1])});
        }
        {
            var Q0;
            {var subQ0=makeQuery(id+"F19.opSweep","SWEPT_FACE",FACE,{"disambiguationData":[OSD([sQuery(id+"F17.wireOp",EDGE,"E89"),sQuery(id+"F18.wireOp",EDGE,"E91.bottom")])]});Q0=makeQuery(id+"F25.opBoolean","MERGE",FACE,{"derivedFrom":[subQ0,makeQuery(id+"F24.opPattern","COPY",FACE,{"derivedFrom":subQ0,"instanceName":"1"})]});}
            var sketch = newSketch(context, id + "F26", { "sketchPlane" : qUnion([Q0])});
            skText(sketch, "E97", { "text": "Big Jim\'s TX", "fontName": "RobotoSlab-Bold.ttf"});
            const initialGuessF26  = {"E97": [0.03032, 0.02516, 1, 0, 0.00537]};
            skSetInitialGuess(sketch, initialGuessF26);
            skSolve(sketch);
        }
        {
            var Q0;
            Q0=qSketchRegion(id+"F26",true);
            extrude(context, id + "F27", {"entities" : qUnion([Q0]), "operationType" : NewBodyOperationType.ADD, "depth" : 2 * mm, "offsetDistance" : 25 * mm, "symmetric" : true});
        }
    });
